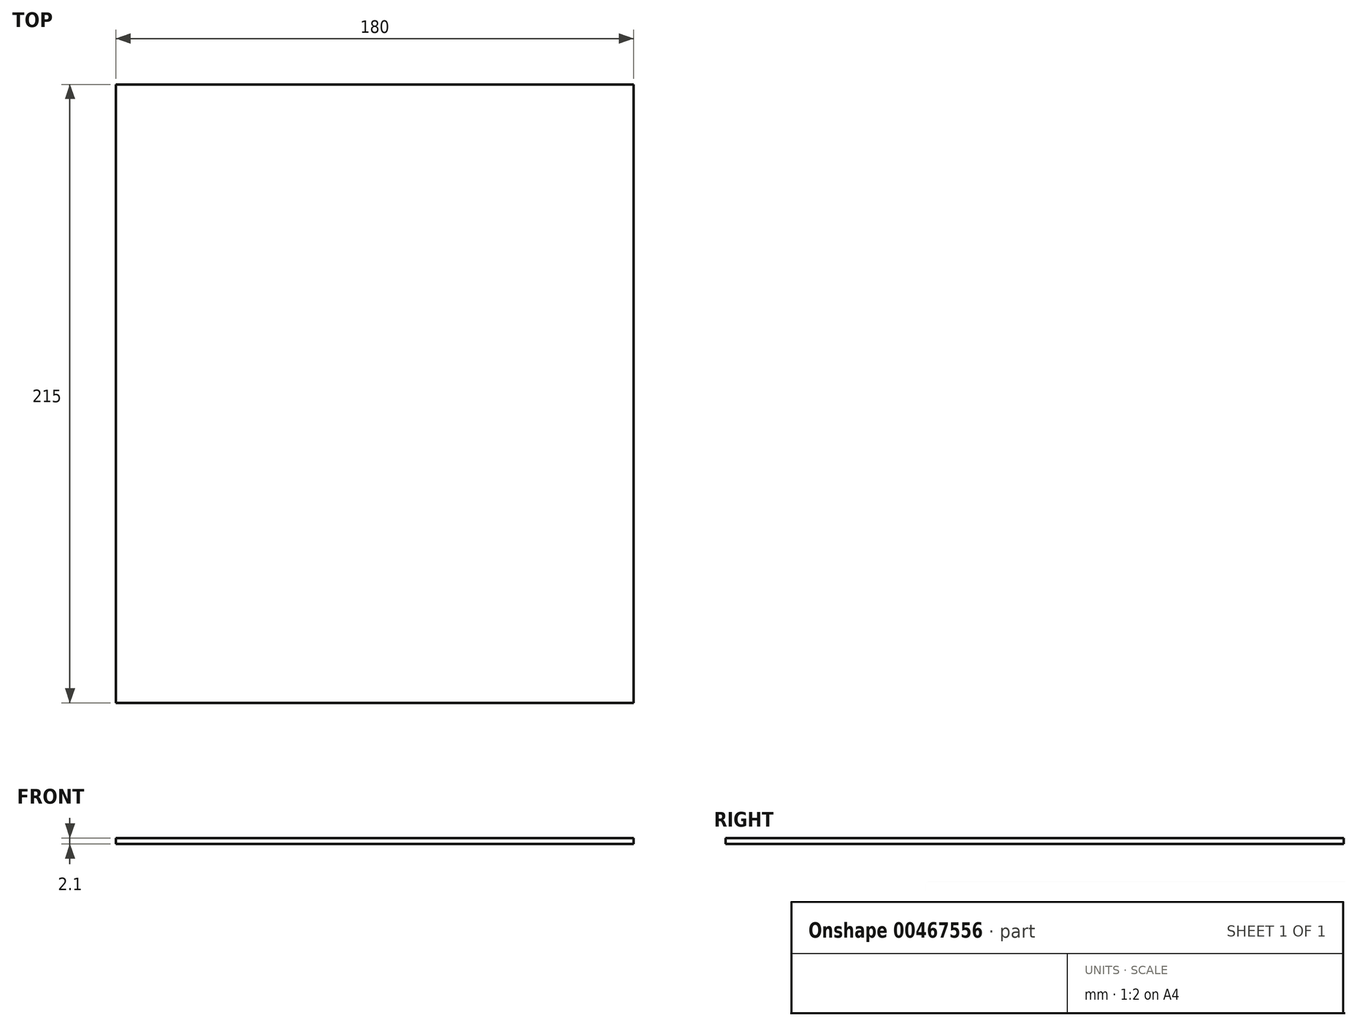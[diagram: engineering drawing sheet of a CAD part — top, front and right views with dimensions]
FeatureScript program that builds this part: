
annotation { "Feature Type Name" : "Feature", "Feature Type Description" : "" }
export const myFeature = defineFeature(function(context is Context, id is Id, definition is map)
    precondition{}
    {
        {
            var Q0;
            Q0=qCreatedBy(makeId("Top.planeOp"),FACE);
            var sketch = newSketch(context, id + "F0", { "sketchPlane" : qUnion([Q0])});
            skLineSegment(sketch, "E0.bottom", {"start": v(0, 0) * mm, "end": v(180, 0) * mm});
            skLineSegment(sketch, "E0.top", {"start": v(0, 215) * mm, "end": v(180, 215) * mm});
            skLineSegment(sketch, "E0.left", {"start": v(0, 0) * mm, "end": v(0, 215) * mm});
            skLineSegment(sketch, "E0.right", {"start": v(180, 0) * mm, "end": v(180, 215) * mm});
            skSolve(sketch);
        }
        {
            var Q0;
            Q0 = qSketchRegion(id + "F0", true);
            extrude(context, id + "F1", {"entities" : qUnion([Q0]), "depth" : 2.1 * mm});
        }
    });
